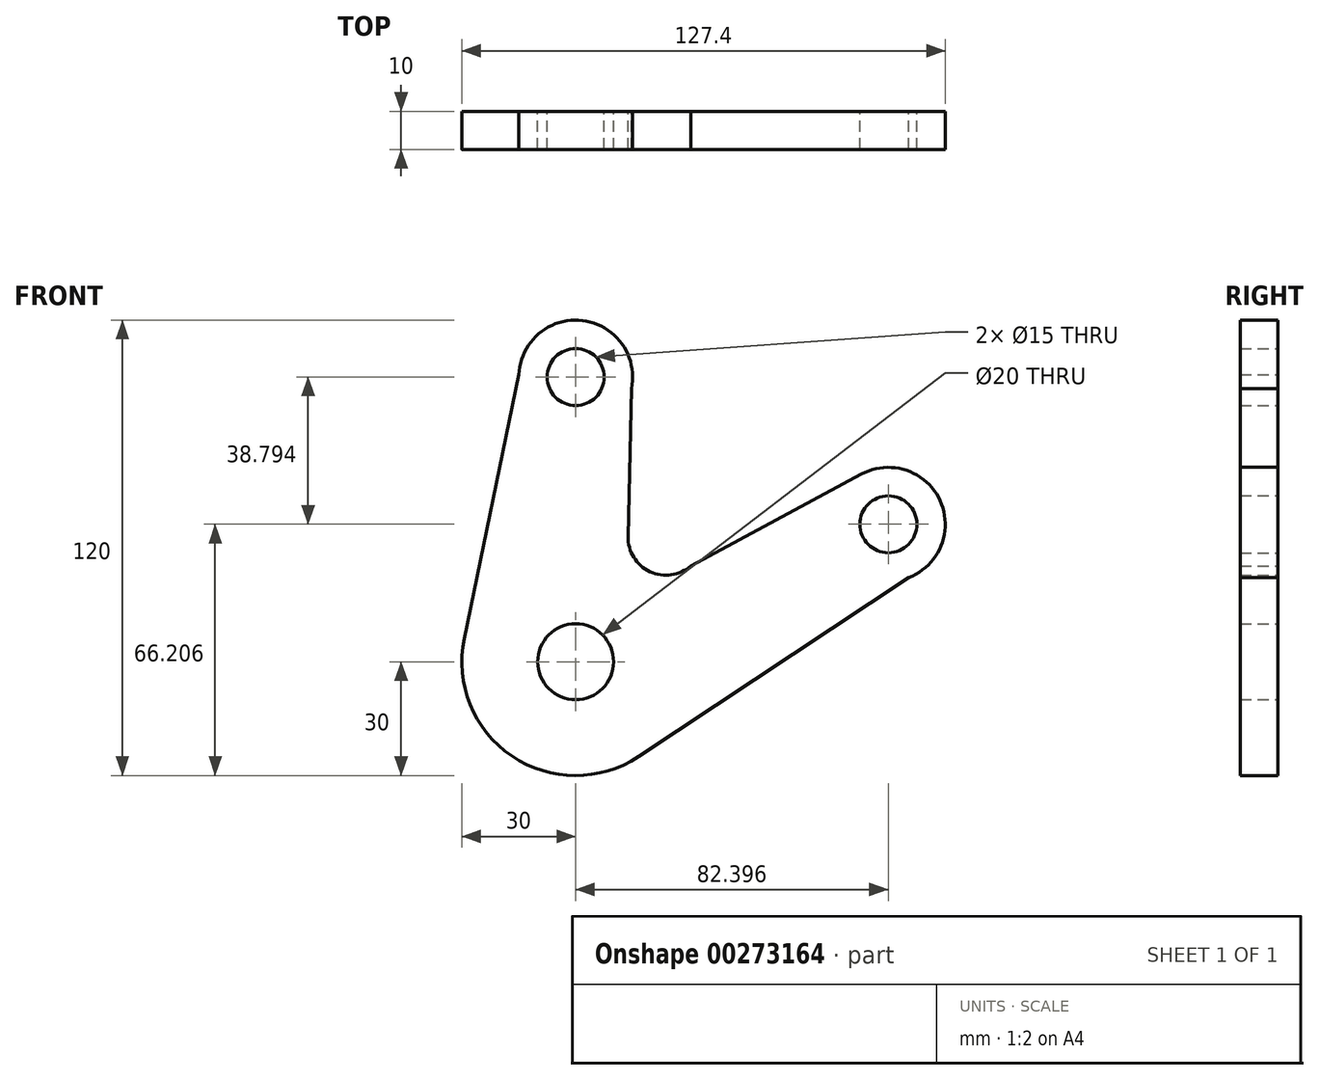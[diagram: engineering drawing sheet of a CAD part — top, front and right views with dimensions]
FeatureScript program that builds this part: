
annotation { "Feature Type Name" : "Feature", "Feature Type Description" : "" }
export const myFeature = defineFeature(function(context is Context, id is Id, definition is map)
    precondition{}
    {
        {
            var Q0;
            Q0=qCreatedBy(makeId("Front.planeOp"),FACE);
            var sketch = newSketch(context, id + "F0", { "sketchPlane" : qUnion([Q0])});
            skCircle(sketch, "E0", {"center": v(0, 0) * mm, "radius": 10 * mm});
            skCircle(sketch, "E1", {"center": v(0, 75) * mm, "radius": 7.5 * mm});
            skCircle(sketch, "E2", {"center": v(82.4, 36.2) * mm, "radius": 7.5 * mm});
            skArc(sketch, "E3", {"start": v(14.7, 71.99) * mm, "mid": v(1.8, 89.9) * mm, "end": v(-14.99, 75.59) * mm});
            skArc(sketch, "E4", {"start": v(-29.38, 6.08) * mm, "mid": v(-16.8, -24.85) * mm, "end": v(16.58, -25) * mm});
            skArc(sketch, "E5", {"start": v(87.76, 22.2) * mm, "mid": v(96.03, 42.45) * mm, "end": v(75.29, 49.42) * mm});
            skLineSegment(sketch, "E6", {"start": v(-14.99, 75.59) * mm, "end": v(-29.38, 6.08) * mm});
            skLineSegment(sketch, "E7", {"start": v(93.21, 25.81) * mm, "end": v(16.58, -25) * mm});
            skArc(sketch, "E8", {"start": v(13.82, 33.02) * mm, "mid": v(19.57, 23.74) * mm, "end": v(30.38, 25.26) * mm});
            skLineSegment(sketch, "E9", {"start": v(30.38, 25.26) * mm, "end": v(75.29, 49.42) * mm});
            skLineSegment(sketch, "E10", {"start": v(14.7, 71.99) * mm, "end": v(13.82, 33.02) * mm});
            skPoint(sketch, "E11.orphan", {"position": v(-30.64, 0) * mm});
            skSolve(sketch);
        }
        {
            var Q0;
            Q0 = qSketchRegion(id + "F0", true);
            extrude(context, id + "F1", {"entities" : qUnion([Q0]), "depth" : 10 * mm});
        }
    });
